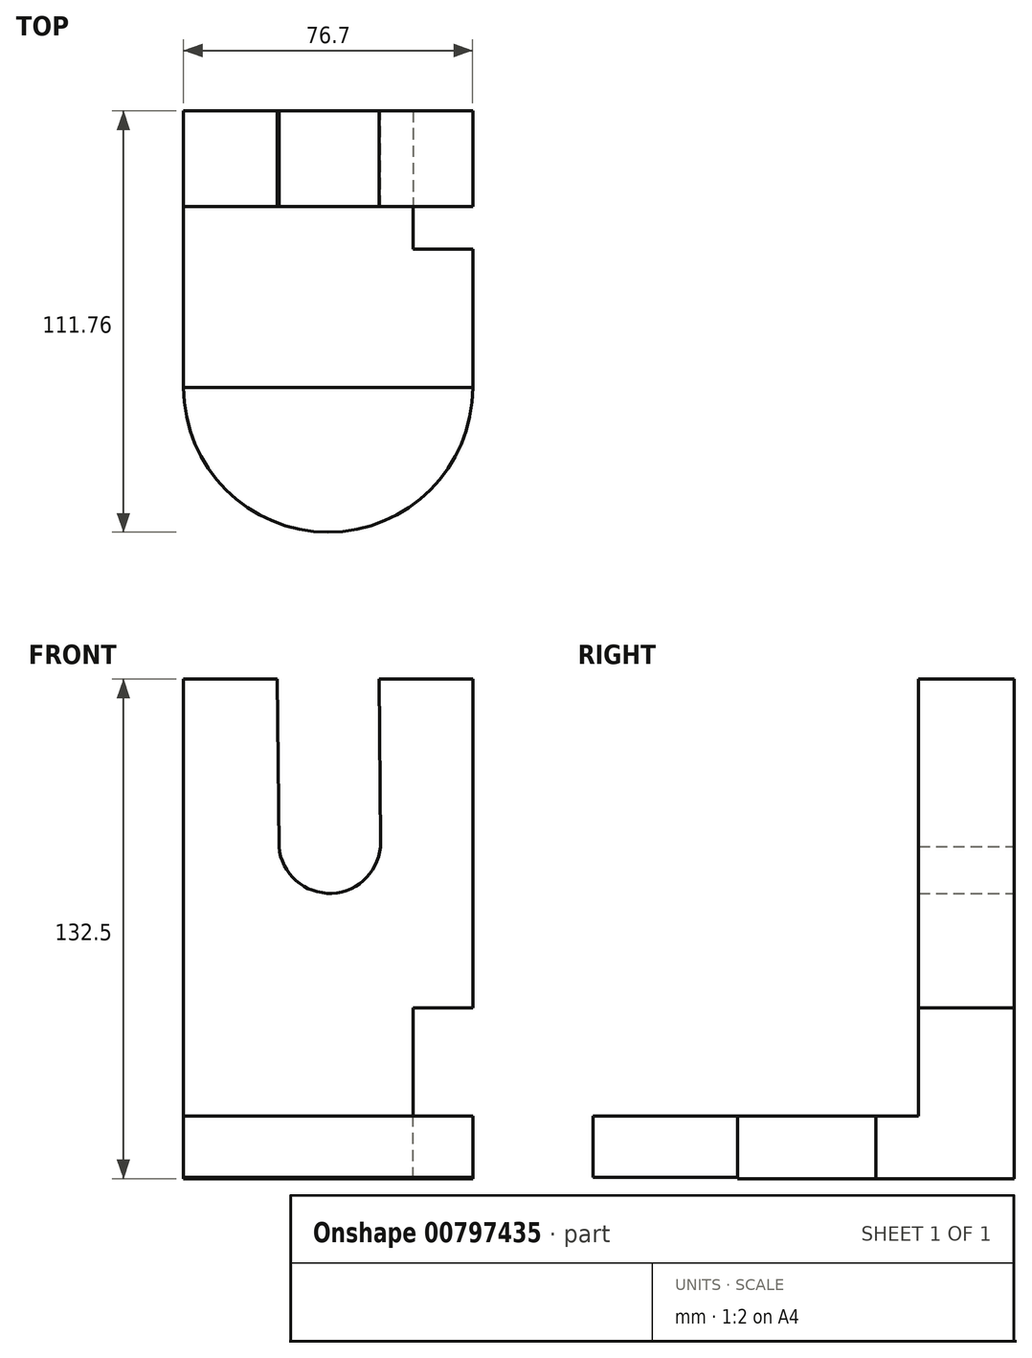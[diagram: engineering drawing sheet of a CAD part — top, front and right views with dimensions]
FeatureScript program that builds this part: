
annotation { "Feature Type Name" : "Feature", "Feature Type Description" : "" }
export const myFeature = defineFeature(function(context is Context, id is Id, definition is map)
    precondition{}
    {
        {
            var Q0;
            Q0=qCreatedBy(makeId("Front.planeOp"),FACE);
            var sketch = newSketch(context, id + "F0", { "sketchPlane" : qUnion([Q0])});
            skLineSegment(sketch, "E0.bottom", {"start": v(-38.04, 67.57) * mm, "end": v(-13.18, 67.57) * mm});
            skLineSegment(sketch, "E0.top", {"start": v(-38.04, -64.93) * mm, "end": v(38.66, -64.93) * mm});
            skLineSegment(sketch, "E0.left", {"start": v(-38.04, 67.57) * mm, "end": v(-38.04, -64.93) * mm});
            skLineSegment(sketch, "E0.right", {"start": v(38.66, 67.57) * mm, "end": v(38.66, -64.93) * mm});
            skLineSegment(sketch, "E1.left", {"start": v(-13.18, 67.57) * mm, "end": v(-12.76, 23.15) * mm});
            skLineSegment(sketch, "E1.right", {"start": v(13.8, 67.57) * mm, "end": v(14.22, 24.4) * mm});
            skArc(sketch, "E2", {"start": v(-12.76, 23.15) * mm, "mid": v(1.33, 10.77) * mm, "end": v(14.22, 24.4) * mm});
            skLineSegment(sketch, "E3.trimOffspring", {"start": v(13.8, 67.57) * mm, "end": v(38.66, 67.57) * mm});
            skLineSegment(sketch, "E4", {"start": v(-38.04, -48.31) * mm, "end": v(38.66, -48.31) * mm});
            skSolve(sketch);
        }
        {
            var Q0;
            {var subQ4=sQuery(id+"F0.wireOp",EDGE,"E0.bottom");Q0=makeQuery(id+"F0.imprint","IMPRINT",FACE,{"disambiguationData":[TD([[makeQuery(id+"F0.imprint","IMPRINT",EDGE,{"derivedFrom":subQ4}),-1.0]])]});}
            var Q1;
            {var subQ0=sQuery(id+"F0.wireOp",EDGE,"E0.top");Q1=makeQuery(id+"F0.imprint","IMPRINT",FACE,{"disambiguationData":[TD([[makeQuery(id+"F0.imprint","IMPRINT",EDGE,{"derivedFrom":subQ0}),1.0]])]});}
            extrude(context, id + "F1", {"entities" : qUnion([Q0, Q1]), "depth" : 25.4 * mm, "offsetDistance" : 25.4 * mm});
        }
        {
            var Q0;
            {var subQ0=sQuery(id+"F0.wireOp",EDGE,"E0.top");Q0=makeQuery(id+"F0.imprint","IMPRINT",FACE,{"disambiguationData":[TD([[makeQuery(id+"F0.imprint","IMPRINT",EDGE,{"derivedFrom":subQ0}),1.0]])]});}
            extrude(context, id + "F2", {"entities" : qUnion([Q0]), "operationType" : NewBodyOperationType.ADD, "depth" : 73.4 * mm, "offsetDistance" : 25.4 * mm});
        }
        {
            var Q0;
            Q0=makeQuery(id+"F2.opExtrude","SWEPT_FACE",FACE,{"disambiguationData":[OSD([sQuery(id+"F0.wireOp",EDGE,"E4")])]});
            var sketch = newSketch(context, id + "F3", { "sketchPlane" : qUnion([Q0])});
            skArc(sketch, "E5", {"start": v(-38.04, -73.4) * mm, "mid": v(0.31, -111.76) * mm, "end": v(38.66, -73.4) * mm});
            skSolve(sketch);
        }
        {
            var Q0;
            Q0 = qSketchRegion(id + "F3", true);
            var Q1;
            Q1=makeQuery(id+"F3.imprint","IMPRINT",FACE,{"disambiguationData":[TD([[makeQuery(id+"F3.imprint","IMPRINT",EDGE,{"derivedFrom":sQuery(id+"F3.wireOp",EDGE,"E5")}),1.0]])]});
            extrude(context, id + "F4", {"entities" : qUnion([Q0, Q1]), "oppositeDirection" : true, "depth" : 16.26 * mm, "offsetDistance" : 25.4 * mm});
        }
        {
            var Q0;
            Q0=makeQuery(id+"F1.opExtrude","CAP_FACE",FACE,{"disambiguationData":[OSD([sQuery(id+"F0.wireOp",EDGE,"E0.bottom"),sQuery(id+"F0.wireOp",EDGE,"E0.top"),sQuery(id+"F0.wireOp",EDGE,"E0.left"),sQuery(id+"F0.wireOp",EDGE,"E0.right"),sQuery(id+"F0.wireOp",EDGE,"E1.left"),sQuery(id+"F0.wireOp",EDGE,"E1.right"),sQuery(id+"F0.wireOp",EDGE,"E2"),sQuery(id+"F0.wireOp",EDGE,"E3.trimOffspring")])],"isStart":false});
            var sketch = newSketch(context, id + "F5", { "sketchPlane" : qUnion([Q0])});
            skLineSegment(sketch, "E6", {"start": v(22.8, -48.31) * mm, "end": v(22.8, -19.66) * mm});
            skLineSegment(sketch, "E7", {"start": v(22.8, -19.66) * mm, "end": v(38.66, -19.66) * mm});
            skLineSegment(sketch, "E8", {"start": v(38.66, -19.66) * mm, "end": v(38.66, -48.31) * mm});
            skLineSegment(sketch, "E9", {"start": v(38.66, -48.31) * mm, "end": v(22.8, -48.31) * mm});
            skSolve(sketch);
        }
        {
            var Q0;
            Q0=makeQuery(id+"F5.imprint","IMPRINT",FACE,{"disambiguationData":[TD([[makeQuery(id+"F5.imprint","IMPRINT",EDGE,{"derivedFrom":sQuery(id+"F5.wireOp",EDGE,"E6")}),-1.0]])]});
            extrude(context, id + "F6", {"entities" : qUnion([Q0]), "operationType" : NewBodyOperationType.REMOVE, "oppositeDirection" : true, "depth" : 177.8 * mm, "offsetDistance" : 25.4 * mm});
        }
        {
            var Q0;
            Q0=makeQuery(id+"F6.boolean.opBoolean","MERGE",FACE,{"derivedFrom":[makeQuery(id+"F2.opExtrude","SWEPT_FACE",FACE,{"disambiguationData":[OSD([sQuery(id+"F0.wireOp",EDGE,"E4")])]}),makeQuery(id+"F6.opExtrude","SWEPT_FACE",FACE,{"disambiguationData":[OSD([sQuery(id+"F5.wireOp",EDGE,"E9")])]})]});
            var sketch = newSketch(context, id + "F7", { "sketchPlane" : qUnion([Q0])});
            skLineSegment(sketch, "E10", {"start": v(22.8, -25.4) * mm, "end": v(22.8, 0) * mm});
            skLineSegment(sketch, "E11", {"start": v(22.8, 0) * mm, "end": v(38.66, 0) * mm});
            skLineSegment(sketch, "E12", {"start": v(38.66, 0) * mm, "end": v(38.66, -36.7) * mm});
            skLineSegment(sketch, "E13", {"start": v(38.66, -36.7) * mm, "end": v(22.8, -36.7) * mm});
            skLineSegment(sketch, "E14", {"start": v(22.8, -36.7) * mm, "end": v(22.8, -25.4) * mm});
            skSolve(sketch);
        }
        {
            var Q0;
            Q0=makeQuery(id+"F7.imprint","IMPRINT",FACE,{"disambiguationData":[TD([[makeQuery(id+"F7.imprint","IMPRINT",EDGE,{"derivedFrom":sQuery(id+"F7.wireOp",EDGE,"E10")}),1.0]])]});
            extrude(context, id + "F8", {"entities" : qUnion([Q0]), "operationType" : NewBodyOperationType.REMOVE, "oppositeDirection" : true, "depth" : 177.8 * mm, "offsetDistance" : 25.4 * mm});
        }
    });
